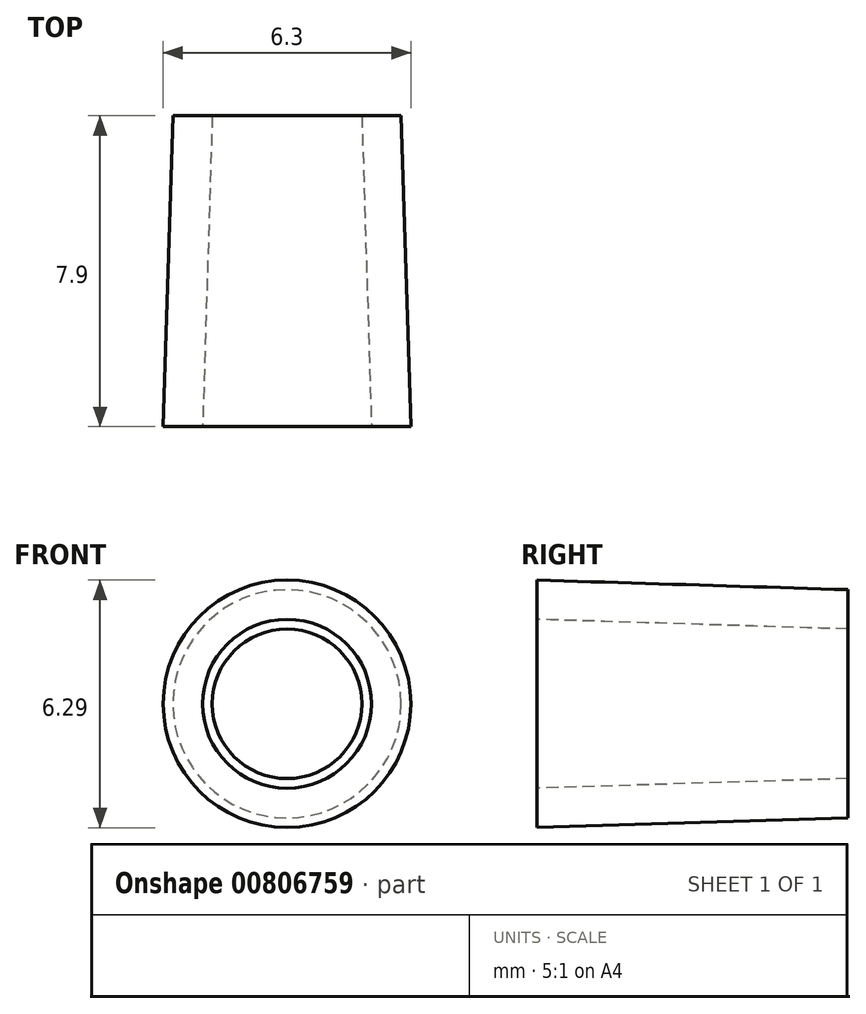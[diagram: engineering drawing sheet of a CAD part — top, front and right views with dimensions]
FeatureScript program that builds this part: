
annotation { "Feature Type Name" : "Feature", "Feature Type Description" : "" }
export const myFeature = defineFeature(function(context is Context, id is Id, definition is map)
    precondition{}
    {
        {
            var Q0;
            Q0=qCreatedBy(makeId("Right.planeOp"),FACE);
            var sketch = newSketch(context, id + "F0", { "sketchPlane" : qUnion([Q0])});
            skLineSegment(sketch, "E0", {"start": v(40.77, -41.83) * mm, "end": v(32.87, -41.83) * mm, "construction": true});
            skPoint(sketch, "E1", {"position": v(40.77, -43.73) * mm});
            skPoint(sketch, "E2", {"position": v(40.77, -44.73) * mm});
            skPoint(sketch, "E3", {"position": v(32.87, -41.83) * mm});
            skPoint(sketch, "E4", {"position": v(32.87, -44.98) * mm});
            skPoint(sketch, "E5", {"position": v(32.87, -43.98) * mm});
            skLineSegment(sketch, "E6", {"start": v(40.77, -43.73) * mm, "end": v(40.77, -44.73) * mm});
            skLineSegment(sketch, "E7", {"start": v(40.77, -44.73) * mm, "end": v(32.87, -44.98) * mm});
            skLineSegment(sketch, "E8", {"start": v(32.87, -43.98) * mm, "end": v(40.77, -43.73) * mm});
            skLineSegment(sketch, "E9", {"start": v(32.87, -43.98) * mm, "end": v(32.87, -44.98) * mm});
            skLineSegment(sketch, "E10", {"start": v(40.77, -41.83) * mm, "end": v(40.77, -44.73) * mm, "construction": true});
            skSolve(sketch);
        }
        {
            var Q0;
            Q0=makeQuery(id+"F0.imprint","IMPRINT",FACE,{"disambiguationData":[TD([[makeQuery(id+"F0.imprint","IMPRINT",EDGE,{"derivedFrom":sQuery(id+"F0.wireOp",EDGE,"E6")}),-1.0]])]});
            var Q1;
            Q1=sQuery(id+"F0.wireOp",EDGE,"E0");
            revolve(context, id + "F1", {"surfaceOperationType" : NewSurfaceOperationType.NEW, "entities" : qUnion([Q0]), "axis" : qUnion([Q1]), "revolveType" : RevolveType.FULL});
        }
    });
